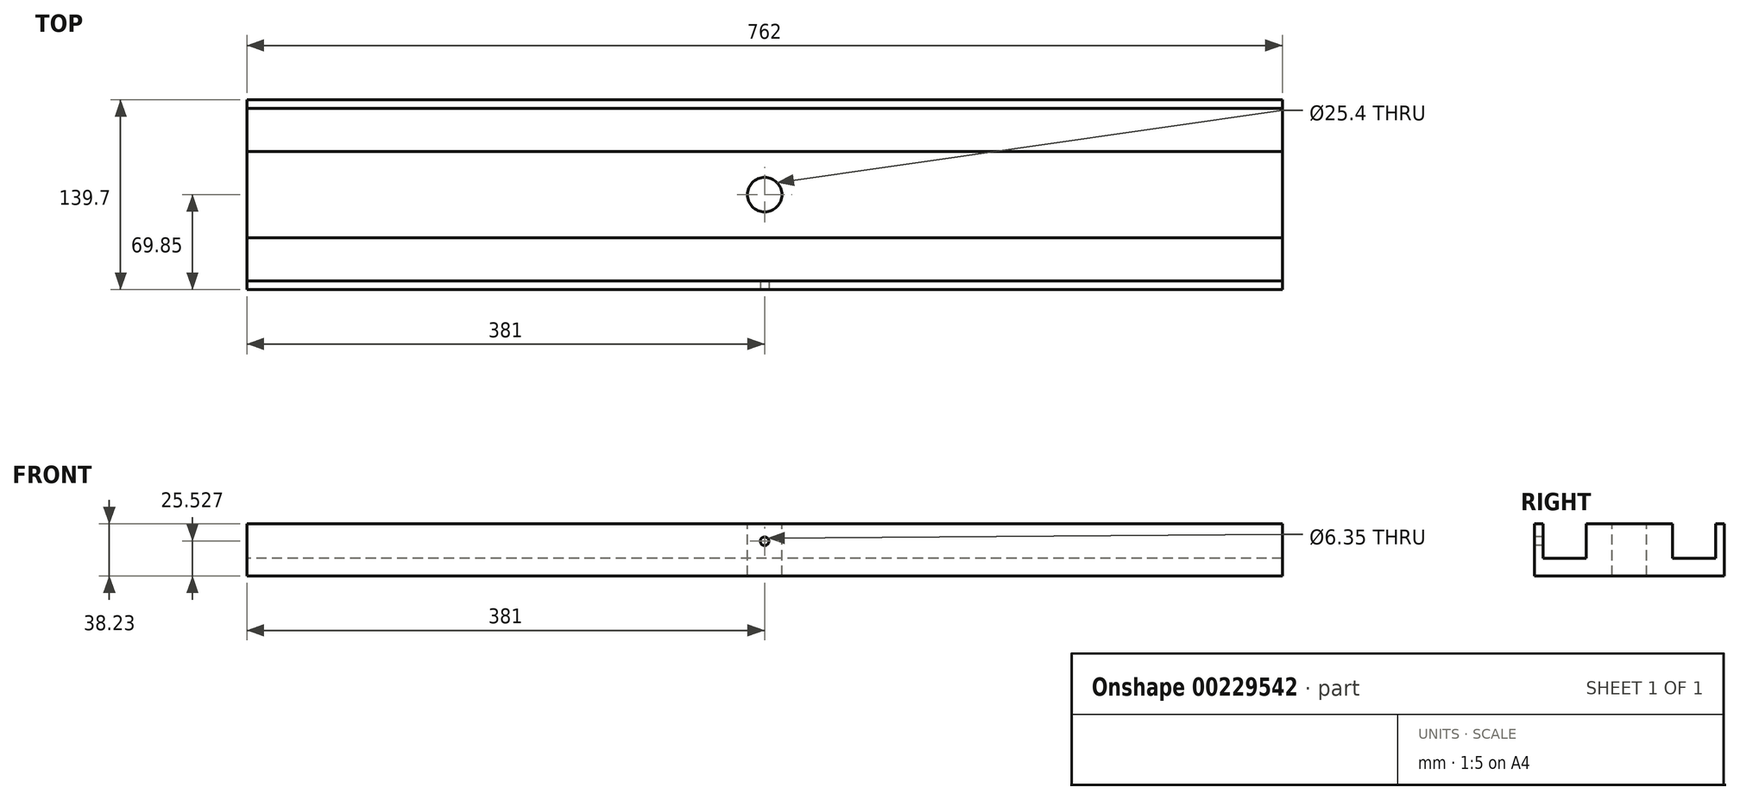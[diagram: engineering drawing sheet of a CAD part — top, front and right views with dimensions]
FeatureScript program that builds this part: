
annotation { "Feature Type Name" : "Feature", "Feature Type Description" : "" }
export const myFeature = defineFeature(function(context is Context, id is Id, definition is map)
    precondition{}
    {
        {
            var Q0;
            Q0=qCreatedBy(makeId("Right.planeOp"),FACE);
            var sketch = newSketch(context, id + "F0", { "sketchPlane" : qUnion([Q0])});
            skLineSegment(sketch, "E0", {"start": v(-69.85, 0) * mm, "end": v(69.85, 0) * mm});
            skLineSegment(sketch, "E1", {"start": v(69.85, 0) * mm, "end": v(69.85, 38.23) * mm});
            skLineSegment(sketch, "E2", {"start": v(69.85, 38.23) * mm, "end": v(63.5, 38.23) * mm});
            skLineSegment(sketch, "E3", {"start": v(63.5, 38.23) * mm, "end": v(63.5, 12.83) * mm});
            skLineSegment(sketch, "E4", {"start": v(63.5, 12.83) * mm, "end": v(31.75, 12.83) * mm});
            skLineSegment(sketch, "E5", {"start": v(31.75, 12.83) * mm, "end": v(31.75, 38.23) * mm});
            skLineSegment(sketch, "E6", {"start": v(31.75, 38.23) * mm, "end": v(-31.75, 38.23) * mm});
            skLineSegment(sketch, "E7", {"start": v(-31.75, 38.23) * mm, "end": v(-31.75, 12.83) * mm});
            skLineSegment(sketch, "E8", {"start": v(-31.75, 12.83) * mm, "end": v(-63.5, 12.83) * mm});
            skLineSegment(sketch, "E9", {"start": v(-63.5, 12.83) * mm, "end": v(-63.5, 38.23) * mm});
            skLineSegment(sketch, "E10", {"start": v(-63.5, 38.23) * mm, "end": v(-69.85, 38.23) * mm});
            skLineSegment(sketch, "E11", {"start": v(-69.85, 38.23) * mm, "end": v(-69.85, 0) * mm});
            skSolve(sketch);
        }
        {
            var Q0;
            Q0 = qSketchRegion(id + "F0", true);
            extrude(context, id + "F1", {"entities" : qUnion([Q0]), "depth" : 381 * mm, "hasSecondDirection" : true, "secondDirectionOppositeDirection" : true, "secondDirectionDepth" : 381 * mm});
        }
        {
            var Q0;
            Q0=makeQuery(id+"F1.opExtrude","SWEPT_FACE",FACE,{"disambiguationData":[OSD([sQuery(id+"F0.wireOp",EDGE,"E11")])]});
            var sketch = newSketch(context, id + "F2", { "sketchPlane" : qUnion([Q0])});
            skPoint(sketch, "E12", {"position": v(0, 25.53) * mm});
            skSolve(sketch);
        }
        {
            var Q0;
            Q0=sQuery(id+"F2.wireOp",VERTEX,"E12");
            var Q1;
            Q1=makeQuery(id+"F1.opExtrude","SWEPT_BODY",BODY,{"disambiguationData":[OSD([sQuery(id+"F0.wireOp",EDGE,"E0"),sQuery(id+"F0.wireOp",EDGE,"E1"),sQuery(id+"F0.wireOp",EDGE,"E2"),sQuery(id+"F0.wireOp",EDGE,"E3"),sQuery(id+"F0.wireOp",EDGE,"E4"),sQuery(id+"F0.wireOp",EDGE,"E5"),sQuery(id+"F0.wireOp",EDGE,"E6"),sQuery(id+"F0.wireOp",EDGE,"E7"),sQuery(id+"F0.wireOp",EDGE,"E8"),sQuery(id+"F0.wireOp",EDGE,"E9"),sQuery(id+"F0.wireOp",EDGE,"E10"),sQuery(id+"F0.wireOp",EDGE,"E11")])]});
            hole(context, id + "F3", {"style" : HoleStyle.SIMPLE, "endStyle" : HoleEndStyle.BLIND, "holeDiameter" : 6.35 * mm, "holeDepth" : 6.35 * mm, "startFromSketch" : true, "locations" : qUnion([Q0]), "scope" : qUnion([Q1])});
        }
        {
            var Q0;
            Q0=makeQuery(id+"F1.opExtrude","SWEPT_FACE",FACE,{"disambiguationData":[OSD([sQuery(id+"F0.wireOp",EDGE,"E6")])]});
            var sketch = newSketch(context, id + "F4", { "sketchPlane" : qUnion([Q0])});
            skPoint(sketch, "E13", {"position": v(0, 0) * mm});
            skSolve(sketch);
        }
        {
            var Q0;
            Q0=sQuery(id+"F4.wireOp",VERTEX,"E13");
            var Q1;
            Q1=makeQuery(id+"F1.opExtrude","SWEPT_BODY",BODY,{"disambiguationData":[OSD([sQuery(id+"F0.wireOp",EDGE,"E0"),sQuery(id+"F0.wireOp",EDGE,"E1"),sQuery(id+"F0.wireOp",EDGE,"E2"),sQuery(id+"F0.wireOp",EDGE,"E3"),sQuery(id+"F0.wireOp",EDGE,"E4"),sQuery(id+"F0.wireOp",EDGE,"E5"),sQuery(id+"F0.wireOp",EDGE,"E6"),sQuery(id+"F0.wireOp",EDGE,"E7"),sQuery(id+"F0.wireOp",EDGE,"E8"),sQuery(id+"F0.wireOp",EDGE,"E9"),sQuery(id+"F0.wireOp",EDGE,"E10"),sQuery(id+"F0.wireOp",EDGE,"E11")])]});
            hole(context, id + "F5", {"style" : HoleStyle.SIMPLE, "endStyle" : HoleEndStyle.THROUGH, "holeDiameter" : 25.4 * mm, "majorDiameter" : 6.35 * mm, "tappedDepth" : 12.7 * mm, "tapClearance" : 3, "locations" : qUnion([Q0]), "scope" : qUnion([Q1])});
        }
    });
